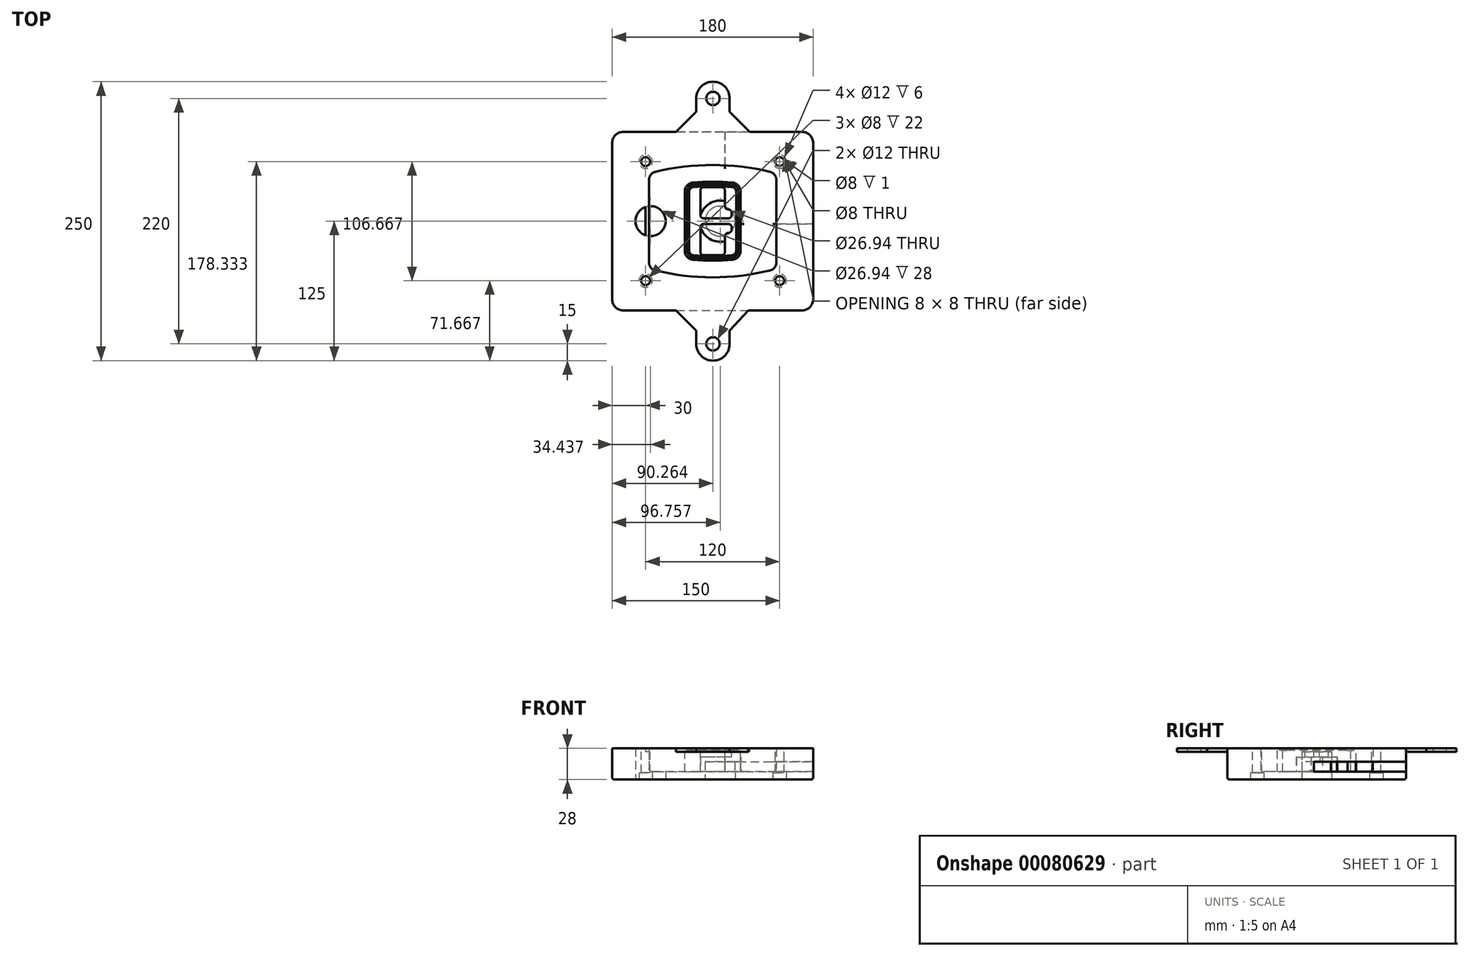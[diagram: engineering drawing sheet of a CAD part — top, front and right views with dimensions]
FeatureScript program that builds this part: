
annotation { "Feature Type Name" : "Feature", "Feature Type Description" : "" }
export const myFeature = defineFeature(function(context is Context, id is Id, definition is map)
    precondition{}
    {
        {
            var Q0;
            Q0=qCreatedBy(makeId("Top.planeOp"),FACE);
            var sketch = newSketch(context, id + "F0", { "sketchPlane" : qUnion([Q0])});
            skPoint(sketch, "E0.rect.middle", {"position": v(0, 0) * mm});
            skLineSegment(sketch, "E1.bottom", {"start": v(-80, -80) * mm, "end": v(80, -80) * mm});
            skLineSegment(sketch, "E1.top", {"start": v(-80, 80) * mm, "end": v(80, 80) * mm});
            skLineSegment(sketch, "E1.left", {"start": v(-90, -70) * mm, "end": v(-90, 70) * mm});
            skLineSegment(sketch, "E1.right", {"start": v(90, -70) * mm, "end": v(90, 70) * mm});
            skLineSegment(sketch, "E2", {"start": v(-90, 80) * mm, "end": v(90, -80) * mm, "construction": true});
            skLineSegment(sketch, "E3", {"start": v(90, 80) * mm, "end": v(-90, -80) * mm, "construction": true});
            skCircle(sketch, "E4", {"center": v(-60, 53.33) * mm, "radius": 4 * mm});
            skCircle(sketch, "E5", {"center": v(60, 53.33) * mm, "radius": 4 * mm});
            skCircle(sketch, "E6", {"center": v(60, -53.33) * mm, "radius": 4 * mm});
            skCircle(sketch, "E7", {"center": v(-60, -53.33) * mm, "radius": 4 * mm});
            skLineSegment(sketch, "E8", {"start": v(-60, 53.33) * mm, "end": v(60, 53.33) * mm, "construction": true});
            skLineSegment(sketch, "E9", {"start": v(60, 53.33) * mm, "end": v(60, -53.33) * mm, "construction": true});
            skLineSegment(sketch, "E10", {"start": v(60, -53.33) * mm, "end": v(-60, -53.33) * mm, "construction": true});
            skLineSegment(sketch, "E11", {"start": v(-60, -53.33) * mm, "end": v(-60, 53.33) * mm, "construction": true});
            skLineSegment(sketch, "E12", {"start": v(-60, 37.3) * mm, "end": v(-60, -37.3) * mm});
            skLineSegment(sketch, "E13", {"start": v(60, 37.3) * mm, "end": v(60, -37.3) * mm});
            skArc(sketch, "E14", {"start": v(52.38, 47.01) * mm, "mid": v(0, 53.33) * mm, "end": v(-52.38, 47.01) * mm});
            skArc(sketch, "E15", {"start": v(-52.38, -47.01) * mm, "mid": v(0, -53.33) * mm, "end": v(52.38, -47.01) * mm});
            skLineSegment(sketch, "E16", {"start": v(-60, 0) * mm, "end": v(60, 0) * mm, "construction": true});
            skPoint(sketch, "E17.visualSharp", {"position": v(-60, -45) * mm});
            skArc(sketch, "E17.filletArc", {"start": v(-60, -37.3) * mm, "mid": v(-57.87, -43.47) * mm, "end": v(-52.38, -47.01) * mm});
            skPoint(sketch, "E18.visualSharp", {"position": v(-60, 45) * mm});
            skArc(sketch, "E18.filletArc", {"start": v(-52.38, 47.01) * mm, "mid": v(-57.87, 43.47) * mm, "end": v(-60, 37.3) * mm});
            skPoint(sketch, "E19.visualSharp", {"position": v(60, 45) * mm});
            skArc(sketch, "E19.filletArc", {"start": v(60, 37.3) * mm, "mid": v(57.87, 43.47) * mm, "end": v(52.38, 47.01) * mm});
            skPoint(sketch, "E20.visualSharp", {"position": v(60, -45) * mm});
            skArc(sketch, "E20.filletArc", {"start": v(52.38, -47.01) * mm, "mid": v(57.87, -43.47) * mm, "end": v(60, -37.3) * mm});
            skPoint(sketch, "E21.visualSharp", {"position": v(-90, 80) * mm});
            skArc(sketch, "E21.filletArc", {"start": v(-80, 80) * mm, "mid": v(-87.07, 77.07) * mm, "end": v(-90, 70) * mm});
            skPoint(sketch, "E22.visualSharp", {"position": v(90, 80) * mm});
            skArc(sketch, "E22.filletArc", {"start": v(90, 70) * mm, "mid": v(87.07, 77.07) * mm, "end": v(80, 80) * mm});
            skPoint(sketch, "E23.visualSharp", {"position": v(90, -80) * mm});
            skArc(sketch, "E23.filletArc", {"start": v(80, -80) * mm, "mid": v(87.07, -77.07) * mm, "end": v(90, -70) * mm});
            skPoint(sketch, "E24.visualSharp", {"position": v(-90, -80) * mm});
            skArc(sketch, "E24.filletArc", {"start": v(-90, -70) * mm, "mid": v(-87.07, -77.07) * mm, "end": v(-80, -80) * mm});
            skArc(sketch, "E25.0", {"start": v(57, 37.3) * mm, "mid": v(55.5, 41.62) * mm, "end": v(51.67, 44.1) * mm});
            skLineSegment(sketch, "E25.1", {"start": v(57, 37.3) * mm, "end": v(57, -37.3) * mm});
            skArc(sketch, "E25.2", {"start": v(51.67, -44.1) * mm, "mid": v(55.5, -41.62) * mm, "end": v(57, -37.3) * mm});
            skArc(sketch, "E25.3", {"start": v(-51.67, -44.1) * mm, "mid": v(0, -50.33) * mm, "end": v(51.67, -44.1) * mm});
            skArc(sketch, "E25.4", {"start": v(-57, -37.3) * mm, "mid": v(-55.5, -41.62) * mm, "end": v(-51.67, -44.1) * mm});
            skArc(sketch, "E25.5", {"start": v(51.67, 44.1) * mm, "mid": v(0, 50.33) * mm, "end": v(-51.67, 44.1) * mm});
            skLineSegment(sketch, "E25.6", {"start": v(-57, 37.3) * mm, "end": v(-57, -37.3) * mm});
            skArc(sketch, "E25.7", {"start": v(-51.67, 44.1) * mm, "mid": v(-55.5, 41.62) * mm, "end": v(-57, 37.3) * mm});
            skArc(sketch, "E26.0", {"start": v(-53.33, 50.9) * mm, "mid": v(-61.01, 45.94) * mm, "end": v(-64, 37.3) * mm});
            skArc(sketch, "E26.1", {"start": v(53.33, 50.9) * mm, "mid": v(0, 57.33) * mm, "end": v(-53.33, 50.9) * mm});
            skArc(sketch, "E26.2", {"start": v(64, 37.3) * mm, "mid": v(61.01, 45.94) * mm, "end": v(53.33, 50.9) * mm});
            skLineSegment(sketch, "E26.3", {"start": v(64, 37.3) * mm, "end": v(64, -37.3) * mm});
            skArc(sketch, "E26.4", {"start": v(53.33, -50.9) * mm, "mid": v(61.01, -45.94) * mm, "end": v(64, -37.3) * mm});
            skLineSegment(sketch, "E26.5", {"start": v(-64, 37.3) * mm, "end": v(-64, -37.3) * mm});
            skArc(sketch, "E26.6", {"start": v(-53.33, -50.9) * mm, "mid": v(0, -57.33) * mm, "end": v(53.33, -50.9) * mm});
            skArc(sketch, "E26.7", {"start": v(-64, -37.3) * mm, "mid": v(-61.01, -45.94) * mm, "end": v(-53.33, -50.9) * mm});
            skSolve(sketch);
        }
        {
            var Q0;
            Q0=makeQuery(id+"F0.imprint","IMPRINT",FACE,{"disambiguationData":[TD([[makeQuery(id+"F0.imprint","IMPRINT",EDGE,{"derivedFrom":sQuery(id+"F0.wireOp",EDGE,"E1.bottom")}),1.0]])]});
            var Q1;
            Q1=makeQuery(id+"F0.imprint","IMPRINT",FACE,{"disambiguationData":[TD([[makeQuery(id+"F0.imprint","IMPRINT",EDGE,{"derivedFrom":sQuery(id+"F0.wireOp",EDGE,"E12")}),1.0]])]});
            var Q2;
            Q2=makeQuery(id+"F0.imprint","IMPRINT",FACE,{"disambiguationData":[TD([[makeQuery(id+"F0.imprint","IMPRINT",EDGE,{"derivedFrom":sQuery(id+"F0.wireOp",EDGE,"E25.0")}),1.0]])]});
            var Q3;
            Q3=makeQuery(id+"F0.imprint","IMPRINT",FACE,{"disambiguationData":[TD([[makeQuery(id+"F0.imprint","IMPRINT",EDGE,{"derivedFrom":sQuery(id+"F0.wireOp",EDGE,"E12")}),-1.0]])]});
            extrude(context, id + "F1", {"entities" : qUnion([Q0, Q1, Q2, Q3]), "oppositeDirection" : true, "depth" : 25 * mm});
        }
        {
            var Q0;
            Q0=makeQuery(id+"F0.imprint","IMPRINT",FACE,{"disambiguationData":[TD([[makeQuery(id+"F0.imprint","IMPRINT",EDGE,{"derivedFrom":sQuery(id+"F0.wireOp",EDGE,"E12")}),1.0]])]});
            extrude(context, id + "F2", {"entities" : qUnion([Q0]), "operationType" : NewBodyOperationType.ADD, "depth" : 3 * mm});
        }
        {
            var Q0;
            Q0=makeQuery(id+"F0.imprint","IMPRINT",FACE,{"disambiguationData":[TD([[makeQuery(id+"F0.imprint","IMPRINT",EDGE,{"derivedFrom":sQuery(id+"F0.wireOp",EDGE,"E25.0")}),1.0]])]});
            extrude(context, id + "F3", {"entities" : qUnion([Q0]), "operationType" : NewBodyOperationType.REMOVE, "oppositeDirection" : true, "depth" : 18 * mm});
        }
        {
            var Q0;
            Q0=makeQuery(id+"F2.opExtrude","CAP_FACE",FACE,{"disambiguationData":[OSD([sQuery(id+"F0.wireOp",EDGE,"E12"),sQuery(id+"F0.wireOp",EDGE,"E13"),sQuery(id+"F0.wireOp",EDGE,"E14"),sQuery(id+"F0.wireOp",EDGE,"E15"),sQuery(id+"F0.wireOp",EDGE,"E17.filletArc"),sQuery(id+"F0.wireOp",EDGE,"E18.filletArc"),sQuery(id+"F0.wireOp",EDGE,"E19.filletArc"),sQuery(id+"F0.wireOp",EDGE,"E20.filletArc"),sQuery(id+"F0.wireOp",EDGE,"E25.0"),sQuery(id+"F0.wireOp",EDGE,"E25.1"),sQuery(id+"F0.wireOp",EDGE,"E25.2"),sQuery(id+"F0.wireOp",EDGE,"E25.3"),sQuery(id+"F0.wireOp",EDGE,"E25.4"),sQuery(id+"F0.wireOp",EDGE,"E25.5"),sQuery(id+"F0.wireOp",EDGE,"E25.6"),sQuery(id+"F0.wireOp",EDGE,"E25.7")])],"isStart":false});
            var sketch = newSketch(context, id + "F4", { "sketchPlane" : qUnion([Q0])});
            skArc(sketch, "E27.0", {"start": v(-17.7, -34.56) * mm, "mid": v(0, -35.33) * mm, "end": v(17.7, -34.56) * mm});
            skArc(sketch, "E28.0", {"start": v(17.7, 34.56) * mm, "mid": v(0, 35.33) * mm, "end": v(-17.7, 34.56) * mm});
            skLineSegment(sketch, "E29", {"start": v(-25, 26.59) * mm, "end": v(-25, -26.59) * mm});
            skLineSegment(sketch, "E30", {"start": v(25, 26.59) * mm, "end": v(25, -26.59) * mm});
            skLineSegment(sketch, "E31", {"start": v(-25, 33.78) * mm, "end": v(25, 33.78) * mm, "construction": true});
            skLineSegment(sketch, "E32", {"start": v(-25, -33.78) * mm, "end": v(25, -33.78) * mm, "construction": true});
            skPoint(sketch, "E33.visualSharp", {"position": v(-25, 33.78) * mm});
            skArc(sketch, "E33.filletArc", {"start": v(-17.7, 34.56) * mm, "mid": v(-22.9, 32) * mm, "end": v(-25, 26.59) * mm});
            skPoint(sketch, "E34.visualSharp", {"position": v(25, 33.78) * mm});
            skArc(sketch, "E34.filletArc", {"start": v(25, 26.59) * mm, "mid": v(22.9, 32) * mm, "end": v(17.7, 34.56) * mm});
            skPoint(sketch, "E35.visualSharp", {"position": v(25, -33.78) * mm});
            skArc(sketch, "E35.filletArc", {"start": v(17.7, -34.56) * mm, "mid": v(22.9, -32) * mm, "end": v(25, -26.59) * mm});
            skPoint(sketch, "E36.visualSharp", {"position": v(-25, -33.78) * mm});
            skArc(sketch, "E36.filletArc", {"start": v(-25, -26.59) * mm, "mid": v(-22.9, -32) * mm, "end": v(-17.7, -34.56) * mm});
            skArc(sketch, "E37.0", {"start": v(51.67, 44.1) * mm, "mid": v(0, 50.33) * mm, "end": v(-51.67, 44.1) * mm});
            skArc(sketch, "E37.1", {"start": v(-51.67, 44.1) * mm, "mid": v(-55.5, 41.62) * mm, "end": v(-57, 37.3) * mm});
            skLineSegment(sketch, "E37.2", {"start": v(-57, 37.3) * mm, "end": v(-57, -37.3) * mm});
            skArc(sketch, "E37.3", {"start": v(-57, -37.3) * mm, "mid": v(-55.5, -41.62) * mm, "end": v(-51.67, -44.1) * mm});
            skArc(sketch, "E37.4", {"start": v(-51.67, -44.1) * mm, "mid": v(0, -50.33) * mm, "end": v(51.67, -44.1) * mm});
            skArc(sketch, "E37.5", {"start": v(51.67, -44.1) * mm, "mid": v(55.5, -41.62) * mm, "end": v(57, -37.3) * mm});
            skLineSegment(sketch, "E37.6", {"start": v(57, 37.3) * mm, "end": v(57, -37.3) * mm});
            skArc(sketch, "E37.7", {"start": v(57, 37.3) * mm, "mid": v(55.5, 41.62) * mm, "end": v(51.67, 44.1) * mm});
            skLineSegment(sketch, "E38.0", {"start": v(23, 26.59) * mm, "end": v(23, -26.59) * mm});
            skArc(sketch, "E38.1", {"start": v(17.53, -32.56) * mm, "mid": v(21.42, -30.64) * mm, "end": v(23, -26.59) * mm});
            skArc(sketch, "E38.2", {"start": v(-17.53, -32.56) * mm, "mid": v(0, -33.33) * mm, "end": v(17.53, -32.56) * mm});
            skArc(sketch, "E38.3", {"start": v(-23, -26.59) * mm, "mid": v(-21.42, -30.64) * mm, "end": v(-17.53, -32.56) * mm});
            skLineSegment(sketch, "E38.4", {"start": v(-23, 26.59) * mm, "end": v(-23, -26.59) * mm});
            skArc(sketch, "E38.5", {"start": v(23, 26.59) * mm, "mid": v(21.42, 30.64) * mm, "end": v(17.53, 32.56) * mm});
            skArc(sketch, "E38.6", {"start": v(-17.53, 32.56) * mm, "mid": v(-21.42, 30.64) * mm, "end": v(-23, 26.59) * mm});
            skArc(sketch, "E38.7", {"start": v(17.53, 32.56) * mm, "mid": v(0, 33.33) * mm, "end": v(-17.53, 32.56) * mm});
            skArc(sketch, "E39.0", {"start": v(21, 26.59) * mm, "mid": v(19.95, 29.29) * mm, "end": v(17.35, 30.57) * mm});
            skLineSegment(sketch, "E39.1", {"start": v(21, 26.59) * mm, "end": v(21, -26.59) * mm});
            skArc(sketch, "E39.2", {"start": v(17.35, -30.57) * mm, "mid": v(19.95, -29.29) * mm, "end": v(21, -26.59) * mm});
            skArc(sketch, "E39.3", {"start": v(-17.35, -30.57) * mm, "mid": v(0, -31.33) * mm, "end": v(17.35, -30.57) * mm});
            skArc(sketch, "E39.4", {"start": v(-21, -26.59) * mm, "mid": v(-19.95, -29.29) * mm, "end": v(-17.35, -30.57) * mm});
            skArc(sketch, "E39.5", {"start": v(17.35, 30.57) * mm, "mid": v(0, 31.33) * mm, "end": v(-17.35, 30.57) * mm});
            skLineSegment(sketch, "E39.6", {"start": v(-21, 26.59) * mm, "end": v(-21, -26.59) * mm});
            skArc(sketch, "E39.7", {"start": v(-17.35, 30.57) * mm, "mid": v(-19.95, 29.29) * mm, "end": v(-21, 26.59) * mm});
            skLineSegment(sketch, "E40", {"start": v(-25, 0) * mm, "end": v(25, 0) * mm, "construction": true});
            skLineSegment(sketch, "E41", {"start": v(-11, 5.5) * mm, "end": v(-11, 27.5) * mm});
            skLineSegment(sketch, "E42", {"start": v(-8, 30.5) * mm, "end": v(8, 30.5) * mm});
            skLineSegment(sketch, "E43", {"start": v(11, 27.5) * mm, "end": v(11, 13.5) * mm});
            skLineSegment(sketch, "E44", {"start": v(14, 10.5) * mm, "end": v(14, 10.5) * mm});
            skLineSegment(sketch, "E45", {"start": v(17, 7.5) * mm, "end": v(17, 5.5) * mm});
            skLineSegment(sketch, "E46", {"start": v(14, 2.5) * mm, "end": v(-8, 2.5) * mm});
            skPoint(sketch, "E47.visualSharp", {"position": v(-11, 30.5) * mm});
            skArc(sketch, "E47.filletArc", {"start": v(-8, 30.5) * mm, "mid": v(-10.12, 29.62) * mm, "end": v(-11, 27.5) * mm});
            skPoint(sketch, "E48.visualSharp", {"position": v(11, 30.5) * mm});
            skArc(sketch, "E48.filletArc", {"start": v(11, 27.5) * mm, "mid": v(10.12, 29.62) * mm, "end": v(8, 30.5) * mm});
            skPoint(sketch, "E49.visualSharp", {"position": v(11, 10.5) * mm});
            skArc(sketch, "E49.filletArc", {"start": v(11, 13.5) * mm, "mid": v(11.88, 11.38) * mm, "end": v(14, 10.5) * mm});
            skPoint(sketch, "E50.visualSharp", {"position": v(17, 10.5) * mm});
            skArc(sketch, "E50.filletArc", {"start": v(17, 7.5) * mm, "mid": v(16.12, 9.62) * mm, "end": v(14, 10.5) * mm});
            skPoint(sketch, "E51.visualSharp", {"position": v(17, 2.5) * mm});
            skArc(sketch, "E51.filletArc", {"start": v(14, 2.5) * mm, "mid": v(16.12, 3.38) * mm, "end": v(17, 5.5) * mm});
            skPoint(sketch, "E52.visualSharp", {"position": v(-11, 2.5) * mm});
            skArc(sketch, "E52.filletArc", {"start": v(-11, 5.5) * mm, "mid": v(-10.12, 3.38) * mm, "end": v(-8, 2.5) * mm});
            skLineSegment(sketch, "E53.0.MirrorCS", {"start": v(14, -2.5) * mm, "end": v(-8, -2.5) * mm});
            skArc(sketch, "E54.0.MirrorCS", {"start": v(-11, -5.5) * mm, "mid": v(-10.12, -3.38) * mm, "end": v(-8, -2.5) * mm});
            skLineSegment(sketch, "E55.0.MirrorCS", {"start": v(-11, -5.5) * mm, "end": v(-11, -27.5) * mm});
            skArc(sketch, "E56.0.MirrorCS", {"start": v(-8, -30.5) * mm, "mid": v(-10.12, -29.62) * mm, "end": v(-11, -27.5) * mm});
            skLineSegment(sketch, "E57.0.MirrorCS", {"start": v(-8, -30.5) * mm, "end": v(8, -30.5) * mm});
            skArc(sketch, "E58.0.MirrorCS", {"start": v(11, -27.5) * mm, "mid": v(10.12, -29.62) * mm, "end": v(8, -30.5) * mm});
            skLineSegment(sketch, "E59.0.MirrorCS", {"start": v(11, -27.5) * mm, "end": v(11, -13.5) * mm});
            skArc(sketch, "E60.0.MirrorCS", {"start": v(11, -13.5) * mm, "mid": v(11.88, -11.38) * mm, "end": v(14, -10.5) * mm});
            skArc(sketch, "E61.0.MirrorCS", {"start": v(17, -7.5) * mm, "mid": v(16.12, -9.62) * mm, "end": v(14, -10.5) * mm});
            skLineSegment(sketch, "E62.0.MirrorCS", {"start": v(17, -7.5) * mm, "end": v(17, -5.5) * mm});
            skArc(sketch, "E63.0.MirrorCS", {"start": v(14, -2.5) * mm, "mid": v(16.12, -3.38) * mm, "end": v(17, -5.5) * mm});
            skSolve(sketch);
        }
        {
            var Q0;
            Q0=makeQuery(id+"F4.imprint","IMPRINT",FACE,{"disambiguationData":[TD([[makeQuery(id+"F4.imprint","IMPRINT",EDGE,{"derivedFrom":sQuery(id+"F4.wireOp",EDGE,"E27.0")}),1.0]])]});
            var Q1;
            Q1=makeQuery(id+"F4.imprint","IMPRINT",FACE,{"disambiguationData":[TD([[makeQuery(id+"F4.imprint","IMPRINT",EDGE,{"derivedFrom":sQuery(id+"F4.wireOp",EDGE,"E38.0")}),-1.0]])]});
            var Q2;
            Q2=makeQuery(id+"F4.imprint","IMPRINT",FACE,{"disambiguationData":[TD([[makeQuery(id+"F4.imprint","IMPRINT",EDGE,{"derivedFrom":sQuery(id+"F4.wireOp",EDGE,"E39.0")}),1.0]])]});
            extrude(context, id + "F5", {"entities" : qUnion([Q0, Q1, Q2]), "operationType" : NewBodyOperationType.ADD, "endBound" : BoundingType.UP_TO_NEXT, "oppositeDirection" : true, "depth" : 25 * mm});
        }
        {
            var Q0;
            Q0=makeQuery(id+"F4.imprint","IMPRINT",FACE,{"disambiguationData":[TD([[makeQuery(id+"F4.imprint","IMPRINT",EDGE,{"derivedFrom":sQuery(id+"F4.wireOp",EDGE,"E38.0")}),-1.0]])]});
            extrude(context, id + "F6", {"entities" : qUnion([Q0]), "operationType" : NewBodyOperationType.REMOVE, "oppositeDirection" : true, "depth" : 2 * mm});
        }
        {
            var Q0;
            Q0=makeQuery(id+"F1.opExtrude","CAP_FACE",FACE,{"disambiguationData":[OSD([sQuery(id+"F0.wireOp",EDGE,"E1.bottom"),sQuery(id+"F0.wireOp",EDGE,"E1.top"),sQuery(id+"F0.wireOp",EDGE,"E1.left"),sQuery(id+"F0.wireOp",EDGE,"E1.right"),sQuery(id+"F0.wireOp",EDGE,"E4"),sQuery(id+"F0.wireOp",EDGE,"E5"),sQuery(id+"F0.wireOp",EDGE,"E6"),sQuery(id+"F0.wireOp",EDGE,"E7"),sQuery(id+"F0.wireOp",EDGE,"E21.filletArc"),sQuery(id+"F0.wireOp",EDGE,"E22.filletArc"),sQuery(id+"F0.wireOp",EDGE,"E23.filletArc"),sQuery(id+"F0.wireOp",EDGE,"E24.filletArc")])],"isStart":false});
            var sketch = newSketch(context, id + "F7", { "sketchPlane" : qUnion([Q0])});
            skCircle(sketch, "E64", {"center": v(6.76, 0) * mm, "radius": 13.47 * mm});
            skCircle(sketch, "E65", {"center": v(-55.56, 0) * mm, "radius": 13.47 * mm});
            skLineSegment(sketch, "E66", {"start": v(90, 0) * mm, "end": v(-90, 0) * mm});
            skCircle(sketch, "E67", {"center": v(6.76, 0) * mm, "radius": 18.47 * mm});
            skCircle(sketch, "E68", {"center": v(60, -53.33) * mm, "radius": 6 * mm});
            skCircle(sketch, "E69", {"center": v(-60, -53.33) * mm, "radius": 6 * mm});
            skCircle(sketch, "E70", {"center": v(-60, 53.33) * mm, "radius": 6 * mm});
            skCircle(sketch, "E71", {"center": v(60, 53.33) * mm, "radius": 6 * mm});
            skSolve(sketch);
        }
        {
            var Q0;
            {var subQ1=sQuery(id+"F7.wireOp",EDGE,"E66");var subQ4=sQuery(id+"F7.wireOp",EDGE,"E64");var subQ6=makeQuery(id+"F7.imprint","INTERSECT",VERTEX,{"disambiguationData":[OD(0.0)],"derivedFrom":[subQ4,subQ1]});Q0=makeQuery(id+"F7.imprint","IMPRINT",FACE,{"disambiguationData":[TD([[makeQuery(id+"F7.imprint","IMPRINT",EDGE,{"disambiguationData":[TD([[subQ6,-1.0]])],"derivedFrom":subQ4}),-1.0]])]});}
            var Q1;
            {var subQ0=sQuery(id+"F7.wireOp",EDGE,"E66");var subQ1=sQuery(id+"F7.wireOp",EDGE,"E64");var subQ3=makeQuery(id+"F7.imprint","INTERSECT",VERTEX,{"disambiguationData":[OD(0.0)],"derivedFrom":[subQ1,subQ0]});Q1=makeQuery(id+"F7.imprint","IMPRINT",FACE,{"disambiguationData":[TD([[makeQuery(id+"F7.imprint","IMPRINT",EDGE,{"disambiguationData":[TD([[subQ3,-1.0]])],"derivedFrom":subQ1}),1.0]])]});}
            var Q2;
            {var subQ0=sQuery(id+"F7.wireOp",EDGE,"E66");var subQ1=sQuery(id+"F7.wireOp",EDGE,"E64");var subQ3=makeQuery(id+"F7.imprint","INTERSECT",VERTEX,{"disambiguationData":[OD(0.0)],"derivedFrom":[subQ1,subQ0]});Q2=makeQuery(id+"F7.imprint","IMPRINT",FACE,{"disambiguationData":[TD([[makeQuery(id+"F7.imprint","IMPRINT",EDGE,{"disambiguationData":[TD([[subQ3,1.0]])],"derivedFrom":subQ1}),1.0]])]});}
            var Q3;
            {var subQ1=sQuery(id+"F7.wireOp",EDGE,"E66");var subQ4=sQuery(id+"F7.wireOp",EDGE,"E64");var subQ6=makeQuery(id+"F7.imprint","INTERSECT",VERTEX,{"disambiguationData":[OD(0.0)],"derivedFrom":[subQ4,subQ1]});Q3=makeQuery(id+"F7.imprint","IMPRINT",FACE,{"disambiguationData":[TD([[makeQuery(id+"F7.imprint","IMPRINT",EDGE,{"disambiguationData":[TD([[subQ6,1.0]])],"derivedFrom":subQ4}),-1.0]])]});}
            extrude(context, id + "F8", {"entities" : qUnion([Q0, Q1, Q2, Q3]), "operationType" : NewBodyOperationType.ADD, "oppositeDirection" : true, "depth" : 20 * mm});
        }
        {
            var Q0;
            {var subQ0=sQuery(id+"F7.wireOp",EDGE,"E66");var subQ1=sQuery(id+"F7.wireOp",EDGE,"E64");var subQ3=makeQuery(id+"F7.imprint","INTERSECT",VERTEX,{"disambiguationData":[OD(0.0)],"derivedFrom":[subQ1,subQ0]});Q0=makeQuery(id+"F7.imprint","IMPRINT",FACE,{"disambiguationData":[TD([[makeQuery(id+"F7.imprint","IMPRINT",EDGE,{"disambiguationData":[TD([[subQ3,-1.0]])],"derivedFrom":subQ1}),1.0]])]});}
            var Q1;
            {var subQ0=sQuery(id+"F7.wireOp",EDGE,"E66");var subQ1=sQuery(id+"F7.wireOp",EDGE,"E64");var subQ3=makeQuery(id+"F7.imprint","INTERSECT",VERTEX,{"disambiguationData":[OD(0.0)],"derivedFrom":[subQ1,subQ0]});Q1=makeQuery(id+"F7.imprint","IMPRINT",FACE,{"disambiguationData":[TD([[makeQuery(id+"F7.imprint","IMPRINT",EDGE,{"disambiguationData":[TD([[subQ3,1.0]])],"derivedFrom":subQ1}),1.0]])]});}
            extrude(context, id + "F9", {"entities" : qUnion([Q0, Q1]), "operationType" : NewBodyOperationType.REMOVE, "oppositeDirection" : true, "depth" : 16 * mm});
        }
        {
            var Q0;
            {var subQ0=sQuery(id+"F7.wireOp",EDGE,"E66");var subQ1=sQuery(id+"F7.wireOp",EDGE,"E65");var subQ3=makeQuery(id+"F7.imprint","INTERSECT",VERTEX,{"disambiguationData":[OD(0.0)],"derivedFrom":[subQ1,subQ0]});Q0=makeQuery(id+"F7.imprint","IMPRINT",FACE,{"disambiguationData":[TD([[makeQuery(id+"F7.imprint","IMPRINT",EDGE,{"disambiguationData":[TD([[subQ3,-1.0]])],"derivedFrom":subQ1}),1.0]])]});}
            var Q1;
            {var subQ0=sQuery(id+"F7.wireOp",EDGE,"E66");var subQ1=sQuery(id+"F7.wireOp",EDGE,"E65");var subQ3=makeQuery(id+"F7.imprint","INTERSECT",VERTEX,{"disambiguationData":[OD(0.0)],"derivedFrom":[subQ1,subQ0]});Q1=makeQuery(id+"F7.imprint","IMPRINT",FACE,{"disambiguationData":[TD([[makeQuery(id+"F7.imprint","IMPRINT",EDGE,{"disambiguationData":[TD([[subQ3,1.0]])],"derivedFrom":subQ1}),1.0]])]});}
            extrude(context, id + "F10", {"entities" : qUnion([Q0, Q1]), "operationType" : NewBodyOperationType.REMOVE, "oppositeDirection" : true, "depth" : 25 * mm});
        }
        {
            var Q0;
            Q0=makeQuery(id+"F7.imprint","IMPRINT",FACE,{"disambiguationData":[TD([[makeQuery(id+"F7.imprint","IMPRINT",EDGE,{"derivedFrom":sQuery(id+"F7.wireOp",EDGE,"E68")}),1.0]])]});
            var Q1;
            Q1=makeQuery(id+"F7.imprint","IMPRINT",FACE,{"disambiguationData":[TD([[makeQuery(id+"F7.imprint","IMPRINT",EDGE,{"derivedFrom":makeQuery(id+"F1.opExtrude","CAP_EDGE",EDGE,{"disambiguationData":[OSD([sQuery(id+"F0.wireOp",EDGE,"E5")])],"isStart":false})}),-1.0]])]});
            var Q2;
            Q2=makeQuery(id+"F7.imprint","IMPRINT",FACE,{"disambiguationData":[TD([[makeQuery(id+"F7.imprint","IMPRINT",EDGE,{"derivedFrom":sQuery(id+"F7.wireOp",EDGE,"E69")}),1.0]])]});
            var Q3;
            Q3=makeQuery(id+"F7.imprint","IMPRINT",FACE,{"disambiguationData":[TD([[makeQuery(id+"F7.imprint","IMPRINT",EDGE,{"derivedFrom":makeQuery(id+"F1.opExtrude","CAP_EDGE",EDGE,{"disambiguationData":[OSD([sQuery(id+"F0.wireOp",EDGE,"E4")])],"isStart":false})}),-1.0]])]});
            var Q4;
            Q4=makeQuery(id+"F7.imprint","IMPRINT",FACE,{"disambiguationData":[TD([[makeQuery(id+"F7.imprint","IMPRINT",EDGE,{"derivedFrom":sQuery(id+"F7.wireOp",EDGE,"E70")}),1.0]])]});
            var Q5;
            Q5=makeQuery(id+"F7.imprint","IMPRINT",FACE,{"disambiguationData":[TD([[makeQuery(id+"F7.imprint","IMPRINT",EDGE,{"derivedFrom":makeQuery(id+"F1.opExtrude","CAP_EDGE",EDGE,{"disambiguationData":[OSD([sQuery(id+"F0.wireOp",EDGE,"E7")])],"isStart":false})}),-1.0]])]});
            var Q6;
            Q6=makeQuery(id+"F7.imprint","IMPRINT",FACE,{"disambiguationData":[TD([[makeQuery(id+"F7.imprint","IMPRINT",EDGE,{"derivedFrom":sQuery(id+"F7.wireOp",EDGE,"E71")}),1.0]])]});
            var Q7;
            Q7=makeQuery(id+"F7.imprint","IMPRINT",FACE,{"disambiguationData":[TD([[makeQuery(id+"F7.imprint","IMPRINT",EDGE,{"derivedFrom":makeQuery(id+"F1.opExtrude","CAP_EDGE",EDGE,{"disambiguationData":[OSD([sQuery(id+"F0.wireOp",EDGE,"E6")])],"isStart":false})}),-1.0]])]});
            extrude(context, id + "F11", {"entities" : qUnion([Q0, Q1, Q2, Q3, Q4, Q5, Q6, Q7]), "operationType" : NewBodyOperationType.REMOVE, "oppositeDirection" : true, "depth" : 6 * mm});
        }
        {
            var Q0;
            Q0=makeQuery(id+"F9.boolean.opBoolean","COPY",FACE,{"derivedFrom":makeQuery(id+"F9.opExtrude","CAP_FACE",FACE,{"disambiguationData":[OSD([sQuery(id+"F7.wireOp",EDGE,"E64")])],"isStart":false})});
            var sketch = newSketch(context, id + "F12", { "sketchPlane" : qUnion([Q0])});
            skArc(sketch, "E72.0", {"start": v(11, -88.19) * mm, "mid": v(97.1, -83.6) * mm, "end": v(92.5, 2.5) * mm});
            skLineSegment(sketch, "E72.1", {"start": v(11, -17.97) * mm, "end": v(11, -17.97) * mm});
            skLineSegment(sketch, "E73", {"start": v(92.5, -105.13) * mm, "end": v(102.3, -105.13) * mm});
            skLineSegment(sketch, "E74.0", {"start": v(92.5, 2.5) * mm, "end": v(14, 2.5) * mm});
            skArc(sketch, "E74.1", {"start": v(14, 2.5) * mm, "mid": v(16.12, 3.38) * mm, "end": v(17, 5.5) * mm});
            skLineSegment(sketch, "E74.2", {"start": v(17, 7.5) * mm, "end": v(17, 5.5) * mm});
            skArc(sketch, "E74.3", {"start": v(17, 7.5) * mm, "mid": v(16.12, 9.62) * mm, "end": v(14, 10.5) * mm});
            skArc(sketch, "E74.4", {"start": v(11, 13.5) * mm, "mid": v(11.88, 11.38) * mm, "end": v(14, 10.5) * mm});
            skLineSegment(sketch, "E74.5", {"start": v(11, 13.5) * mm, "end": v(11, -88.19) * mm});
            skLineSegment(sketch, "E74.7", {"start": v(92.5, -2.5) * mm, "end": v(14, -2.5) * mm});
            skArc(sketch, "E74.8", {"start": v(14, -2.5) * mm, "mid": v(16.12, -3.38) * mm, "end": v(17, -5.5) * mm});
            skLineSegment(sketch, "E74.9", {"start": v(17, -7.5) * mm, "end": v(17, -5.5) * mm});
            skArc(sketch, "E74.10", {"start": v(17, -7.5) * mm, "mid": v(16.12, -9.62) * mm, "end": v(14, -10.5) * mm});
            skArc(sketch, "E74.11", {"start": v(11, -13.5) * mm, "mid": v(11.88, -11.38) * mm, "end": v(14, -10.5) * mm});
            skLineSegment(sketch, "E74.12", {"start": v(11, -17.97) * mm, "end": v(11, -13.5) * mm});
            skPoint(sketch, "E75.orphan", {"position": v(11, -27.5) * mm});
            skPoint(sketch, "E76.orphan", {"position": v(-8, -2.5) * mm});
            skPoint(sketch, "E77.orphan", {"position": v(-8, 2.5) * mm});
            skPoint(sketch, "E78.orphan", {"position": v(11, 27.5) * mm});
            skSolve(sketch);
        }
        {
            var Q0;
            {var subQ7=sQuery(id+"F12.wireOp",EDGE,"E72.0");var subQ14=sQuery(id+"F12.wireOp",EDGE,"E72.1");var subQ16=sQuery(id+"F12.wireOp",EDGE,"E74.1");var subQ18=sQuery(id+"F12.wireOp",EDGE,"E74.8");Q0=qUnion([makeQuery(id+"F12.imprint","IMPRINT",FACE,{"disambiguationData":[TD([[makeQuery(id+"F12.imprint","IMPRINT",EDGE,{"derivedFrom":subQ7}),1.0]])]}),makeQuery(id+"F12.imprint","IMPRINT",FACE,{"disambiguationData":[TD([[makeQuery(id+"F12.imprint","IMPRINT",EDGE,{"derivedFrom":subQ14}),1.0]])]}),makeQuery(id+"F12.imprint","IMPRINT",FACE,{"disambiguationData":[TD([[makeQuery(id+"F12.imprint","IMPRINT",EDGE,{"derivedFrom":subQ16}),1.0]])]}),makeQuery(id+"F12.imprint","IMPRINT",FACE,{"disambiguationData":[TD([[makeQuery(id+"F12.imprint","IMPRINT",EDGE,{"derivedFrom":subQ18}),-1.0]])]})]);}
            var Q1;
            Q1=makeQuery(id+"F5.boolean.opBoolean","SPLIT",FACE,{"disambiguationData":[TD([makeQuery(id+"F5.opExtrude","SWEPT_FACE",FACE,{"disambiguationData":[OSD([sQuery(id+"F4.wireOp",EDGE,"E41")])]})])],"derivedFrom":makeQuery(id+"F3.boolean.opBoolean","COPY",FACE,{"derivedFrom":makeQuery(id+"F3.opExtrude","CAP_FACE",FACE,{"disambiguationData":[OSD([sQuery(id+"F0.wireOp",EDGE,"E25.0"),sQuery(id+"F0.wireOp",EDGE,"E25.1"),sQuery(id+"F0.wireOp",EDGE,"E25.2"),sQuery(id+"F0.wireOp",EDGE,"E25.3"),sQuery(id+"F0.wireOp",EDGE,"E25.4"),sQuery(id+"F0.wireOp",EDGE,"E25.5"),sQuery(id+"F0.wireOp",EDGE,"E25.6"),sQuery(id+"F0.wireOp",EDGE,"E25.7")])],"isStart":false})})});
            extrude(context, id + "F13", {"entities" : qUnion([Q0]), "operationType" : NewBodyOperationType.REMOVE, "endBound" : BoundingType.UP_TO_SURFACE, "endBoundEntityFace" : qUnion([Q1]), "depth" : 25 * mm});
        }
        {
            var Q0;
            Q0=makeQuery(id+"F3.boolean.opBoolean","COPY",EDGE,{"derivedFrom":makeQuery(id+"F3.opExtrude","CAP_EDGE",EDGE,{"disambiguationData":[OSD([sQuery(id+"F0.wireOp",EDGE,"E25.6")])],"isStart":false})});
            var Q1;
            Q1=makeQuery(id+"F8.boolean.opBoolean","INTERSECT",EDGE,{"derivedFrom":[makeQuery(id+"F5.opExtrude","SWEPT_FACE",FACE,{"disambiguationData":[OSD([sQuery(id+"F4.wireOp",EDGE,"E30")])]}),makeQuery(id+"F8.opExtrude","CAP_FACE",FACE,{"disambiguationData":[OSD([sQuery(id+"F7.wireOp",EDGE,"E67")])],"isStart":false})]});
            var Q2;
            Q2=makeQuery(id+"F8.boolean.opBoolean","INTERSECT",EDGE,{"disambiguationData":[OD(1.0)],"derivedFrom":[makeQuery(id+"F5.opExtrude","SWEPT_FACE",FACE,{"disambiguationData":[OSD([sQuery(id+"F4.wireOp",EDGE,"E30")])]}),makeQuery(id+"F8.opExtrude","SWEPT_FACE",FACE,{"disambiguationData":[OSD([sQuery(id+"F7.wireOp",EDGE,"E67")])]})]});
            var Q3;
            {var subQ0=makeQuery(id+"F3.boolean.opBoolean","COPY",FACE,{"derivedFrom":makeQuery(id+"F3.opExtrude","CAP_FACE",FACE,{"disambiguationData":[OSD([sQuery(id+"F0.wireOp",EDGE,"E25.0"),sQuery(id+"F0.wireOp",EDGE,"E25.1"),sQuery(id+"F0.wireOp",EDGE,"E25.2"),sQuery(id+"F0.wireOp",EDGE,"E25.3"),sQuery(id+"F0.wireOp",EDGE,"E25.4"),sQuery(id+"F0.wireOp",EDGE,"E25.5"),sQuery(id+"F0.wireOp",EDGE,"E25.6"),sQuery(id+"F0.wireOp",EDGE,"E25.7")])],"isStart":false})});var subQ1=sQuery(id+"F4.wireOp",EDGE,"E30");Q3=makeQuery(id+"F8.boolean.opBoolean","SPLIT",EDGE,{"disambiguationData":[TD([makeQuery(id+"F5.opExtrude","SWEPT_FACE",FACE,{"disambiguationData":[OSD([sQuery(id+"F4.wireOp",EDGE,"E35.filletArc")])]})])],"derivedFrom":makeQuery(id+"F5.opExtrude","TWEAK_EDGE",EDGE,{"derivedFrom":[subQ0,makeQuery(id+"F4.imprint","IMPRINT",EDGE,{"derivedFrom":subQ1})]})});}
            var Q4;
            {var subQ0=sQuery(id+"F0.wireOp",EDGE,"E25.0");var subQ1=sQuery(id+"F0.wireOp",EDGE,"E25.1");var subQ2=sQuery(id+"F0.wireOp",EDGE,"E25.2");var subQ3=sQuery(id+"F0.wireOp",EDGE,"E25.3");var subQ4=sQuery(id+"F0.wireOp",EDGE,"E25.4");var subQ5=sQuery(id+"F0.wireOp",EDGE,"E25.5");var subQ6=sQuery(id+"F0.wireOp",EDGE,"E25.6");var subQ7=sQuery(id+"F0.wireOp",EDGE,"E25.7");Q4=makeQuery(id+"F8.boolean.opBoolean","INTERSECT",EDGE,{"derivedFrom":[makeQuery(id+"F5.boolean.opBoolean","SPLIT",FACE,{"disambiguationData":[TD([makeQuery(id+"F2.opExtrude","SWEPT_FACE",FACE,{"disambiguationData":[OSD([subQ0])]})])],"derivedFrom":makeQuery(id+"F3.boolean.opBoolean","COPY",FACE,{"derivedFrom":makeQuery(id+"F3.opExtrude","CAP_FACE",FACE,{"disambiguationData":[OSD([subQ0,subQ1,subQ2,subQ3,subQ4,subQ5,subQ6,subQ7])],"isStart":false})})}),makeQuery(id+"F8.opExtrude","SWEPT_FACE",FACE,{"disambiguationData":[OSD([sQuery(id+"F7.wireOp",EDGE,"E67")])]})]});}
            var Q5;
            Q5=makeQuery(id+"F8.boolean.opBoolean","INTERSECT",EDGE,{"disambiguationData":[OD(0.0)],"derivedFrom":[makeQuery(id+"F5.opExtrude","SWEPT_FACE",FACE,{"disambiguationData":[OSD([sQuery(id+"F4.wireOp",EDGE,"E30")])]}),makeQuery(id+"F8.opExtrude","SWEPT_FACE",FACE,{"disambiguationData":[OSD([sQuery(id+"F7.wireOp",EDGE,"E67")])]})]});
            fillet(context, id + "F14", {"entities" : qUnion([Q0, Q1, Q2, Q3, Q4, Q5]), "radius" : 3 * mm, "tangentPropagation" : true, "allowEdgeOverflow" : false});
        }
        {
            var Q0;
            Q0=makeQuery(id+"F1.opExtrude","CAP_EDGE",EDGE,{"disambiguationData":[OSD([sQuery(id+"F0.wireOp",EDGE,"E1.bottom")])],"isStart":false});
            fillet(context, id + "F15", {"entities" : qUnion([Q0]), "radius" : 2 * mm, "tangentPropagation" : true, "allowEdgeOverflow" : false});
        }
        {
            var Q0;
            {var subQ0=sQuery(id+"F0.wireOp",EDGE,"E22.filletArc");var subQ1=sQuery(id+"F0.wireOp",EDGE,"E7");var subQ2=sQuery(id+"F0.wireOp",EDGE,"E6");var subQ3=sQuery(id+"F0.wireOp",EDGE,"E5");var subQ4=sQuery(id+"F0.wireOp",EDGE,"E4");var subQ5=sQuery(id+"F0.wireOp",EDGE,"E1.bottom");var subQ6=sQuery(id+"F0.wireOp",EDGE,"E21.filletArc");var subQ7=sQuery(id+"F0.wireOp",EDGE,"E1.top");var subQ8=sQuery(id+"F0.wireOp",EDGE,"E1.left");var subQ9=sQuery(id+"F0.wireOp",EDGE,"E1.right");var subQ10=sQuery(id+"F0.wireOp",EDGE,"E23.filletArc");var subQ11=sQuery(id+"F0.wireOp",EDGE,"E24.filletArc");Q0=makeQuery(id+"F2.boolean.opBoolean","SPLIT",FACE,{"disambiguationData":[TD([makeQuery(id+"F1.opExtrude","SWEPT_FACE",FACE,{"disambiguationData":[OSD([subQ5])]})])],"derivedFrom":makeQuery(id+"F1.opExtrude","CAP_FACE",FACE,{"disambiguationData":[OSD([subQ5,subQ7,subQ8,subQ9,subQ4,subQ3,subQ2,subQ1,subQ6,subQ0,subQ10,subQ11])],"isStart":true})});}
            var sketch = newSketch(context, id + "F16", { "sketchPlane" : qUnion([Q0])});
            skLineSegment(sketch, "E79", {"start": v(-14.74, 98) * mm, "end": v(-14.74, 110) * mm});
            skLineSegment(sketch, "E80", {"start": v(33.26, 80) * mm, "end": v(15.26, 98) * mm});
            skLineSegment(sketch, "E81", {"start": v(15.26, 110) * mm, "end": v(15.26, 98) * mm});
            skArc(sketch, "E82", {"start": v(15.26, 110) * mm, "mid": v(0.26, 125) * mm, "end": v(-14.74, 110) * mm});
            skCircle(sketch, "E83", {"center": v(0.26, 110) * mm, "radius": 6 * mm});
            skLineSegment(sketch, "E84", {"start": v(0.26, 110) * mm, "end": v(0.26, 80) * mm, "construction": true});
            skLineSegment(sketch, "E85", {"start": v(-90, 0) * mm, "end": v(90, 0) * mm, "construction": true});
            skLineSegment(sketch, "E86.MirrorCS", {"start": v(15.26, 98) * mm, "end": v(15.26, 110) * mm});
            skLineSegment(sketch, "E87.MirrorCS", {"start": v(-32.74, 80) * mm, "end": v(-14.74, 98) * mm});
            skLineSegment(sketch, "E88.MirrorCS", {"start": v(-14.74, 110) * mm, "end": v(-14.74, 98) * mm});
            skArc(sketch, "E89.MirrorCS", {"start": v(-14.74, 110) * mm, "mid": v(0.26, 125) * mm, "end": v(15.26, 110) * mm});
            skLineSegment(sketch, "E90.MirrorCS", {"start": v(32.06, -80) * mm, "end": v(15.26, -98) * mm});
            skLineSegment(sketch, "E91.MirrorCS", {"start": v(15.26, -98) * mm, "end": v(15.26, -110) * mm});
            skArc(sketch, "E92.MirrorCS", {"start": v(15.26, -110) * mm, "mid": v(0.26, -125) * mm, "end": v(-14.74, -110) * mm});
            skLineSegment(sketch, "E93.MirrorCS", {"start": v(-14.74, -110) * mm, "end": v(-14.74, -98) * mm});
            skLineSegment(sketch, "E94.MirrorCS", {"start": v(-32.74, -80) * mm, "end": v(-14.74, -98) * mm});
            skLineSegment(sketch, "E95.MirrorCS", {"start": v(0.26, -110) * mm, "end": v(0.26, -80) * mm, "construction": true});
            skCircle(sketch, "E96.MirrorC", {"center": v(0.26, -110) * mm, "radius": 6 * mm});
            skSolve(sketch);
        }
        {
            var Q0;
            {var subQ1=sQuery(id+"F16.wireOp",EDGE,"E80");Q0=makeQuery(id+"F16.imprint","IMPRINT",FACE,{"disambiguationData":[TD([[makeQuery(id+"F16.imprint","IMPRINT",EDGE,{"derivedFrom":subQ1}),1.0]])]});}
            var Q1;
            Q1=makeQuery(id+"F16.imprint","IMPRINT",FACE,{"disambiguationData":[TD([[makeQuery(id+"F16.imprint","IMPRINT",EDGE,{"derivedFrom":sQuery(id+"F16.wireOp",EDGE,"E91.MirrorCS")}),-1.0]])]});
            var Q2;
            Q2=makeQuery(id+"F16.imprint","IMPRINT",FACE,{"disambiguationData":[TD([[makeQuery(id+"F16.imprint","IMPRINT",EDGE,{"derivedFrom":makeQuery(id+"F1.opExtrude","CAP_EDGE",EDGE,{"disambiguationData":[OSD([sQuery(id+"F0.wireOp",EDGE,"E1.left")])],"isStart":true})}),-1.0]])]});
            var Q3;
            Q3=makeQuery(id+"F2.opExtrude","CAP_FACE",FACE,{"disambiguationData":[OSD([sQuery(id+"F0.wireOp",EDGE,"E12"),sQuery(id+"F0.wireOp",EDGE,"E13"),sQuery(id+"F0.wireOp",EDGE,"E14"),sQuery(id+"F0.wireOp",EDGE,"E15"),sQuery(id+"F0.wireOp",EDGE,"E17.filletArc"),sQuery(id+"F0.wireOp",EDGE,"E18.filletArc"),sQuery(id+"F0.wireOp",EDGE,"E19.filletArc"),sQuery(id+"F0.wireOp",EDGE,"E20.filletArc"),sQuery(id+"F0.wireOp",EDGE,"E25.0"),sQuery(id+"F0.wireOp",EDGE,"E25.1"),sQuery(id+"F0.wireOp",EDGE,"E25.2"),sQuery(id+"F0.wireOp",EDGE,"E25.3"),sQuery(id+"F0.wireOp",EDGE,"E25.4"),sQuery(id+"F0.wireOp",EDGE,"E25.5"),sQuery(id+"F0.wireOp",EDGE,"E25.6"),sQuery(id+"F0.wireOp",EDGE,"E25.7")])],"isStart":false});
            extrude(context, id + "F17", {"entities" : qUnion([Q0, Q1, Q2]), "operationType" : NewBodyOperationType.ADD, "endBound" : BoundingType.UP_TO_SURFACE, "endBoundEntityFace" : qUnion([Q3]), "depth" : 25 * mm});
        }
    });
